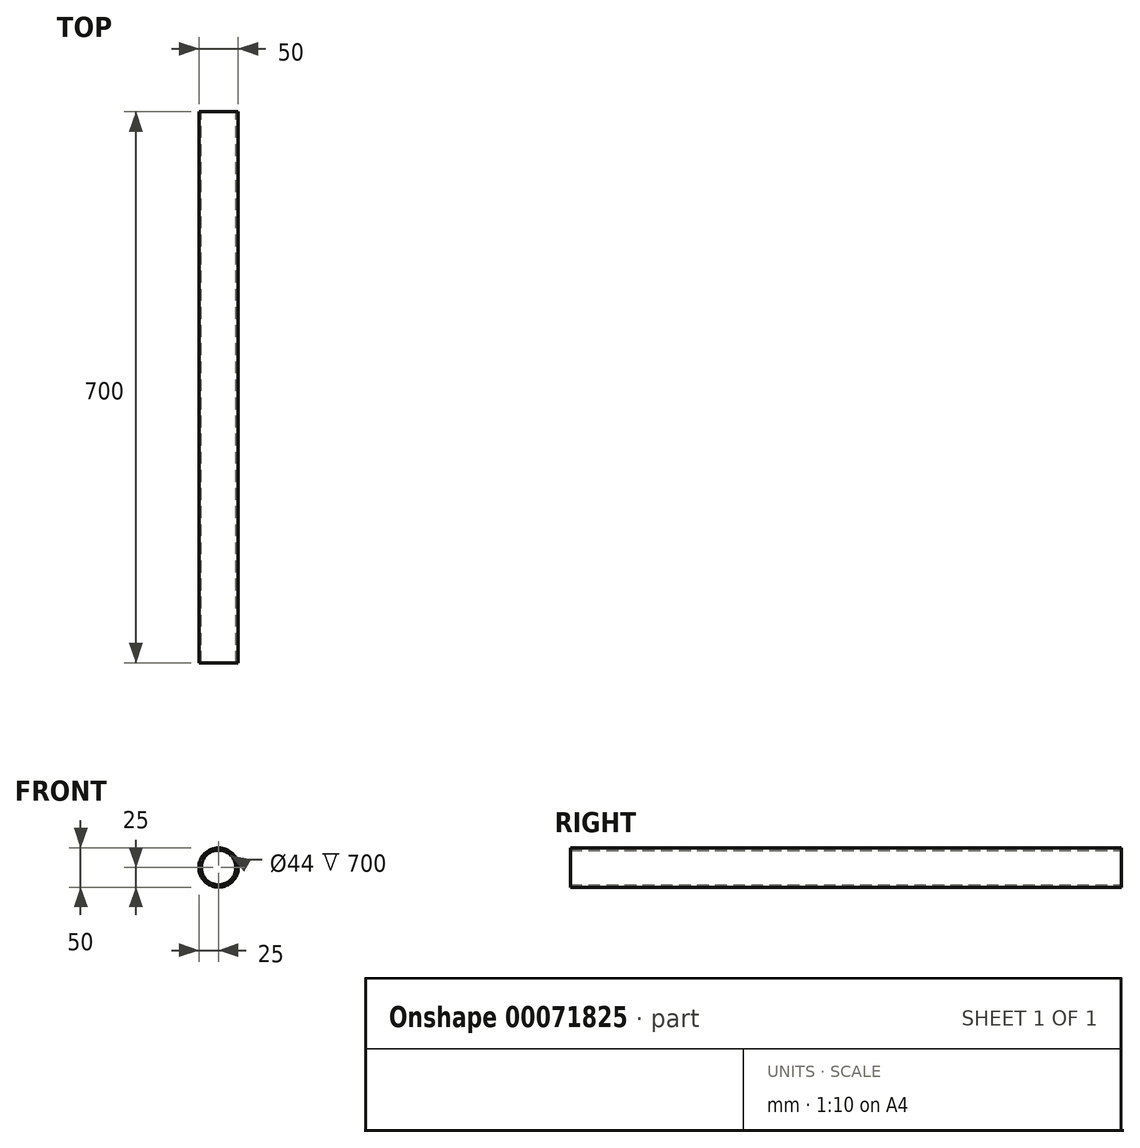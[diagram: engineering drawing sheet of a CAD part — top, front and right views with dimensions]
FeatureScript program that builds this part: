
annotation { "Feature Type Name" : "Feature", "Feature Type Description" : "" }
export const myFeature = defineFeature(function(context is Context, id is Id, definition is map)
    precondition{}
    {
        {
            var Q0;
            Q0=qCreatedBy(makeId("Front.planeOp"),FACE);
            var sketch = newSketch(context, id + "F0", { "sketchPlane" : qUnion([Q0])});
            skCircle(sketch, "E0", {"center": v(0, 0) * mm, "radius": 25 * mm});
            skCircle(sketch, "E1", {"center": v(0, 0) * mm, "radius": 22 * mm});
            skSolve(sketch);
        }
        {
            var Q0;
            Q0=makeQuery(id+"F0.imprint","IMPRINT",FACE,{"disambiguationData":[TD([[makeQuery(id+"F0.imprint","IMPRINT",EDGE,{"derivedFrom":sQuery(id+"F0.wireOp",EDGE,"E0")}),1.0]])]});
            extrude(context, id + "F1", {"entities" : qUnion([Q0]), "depth" : 700 * mm});
        }
    });
